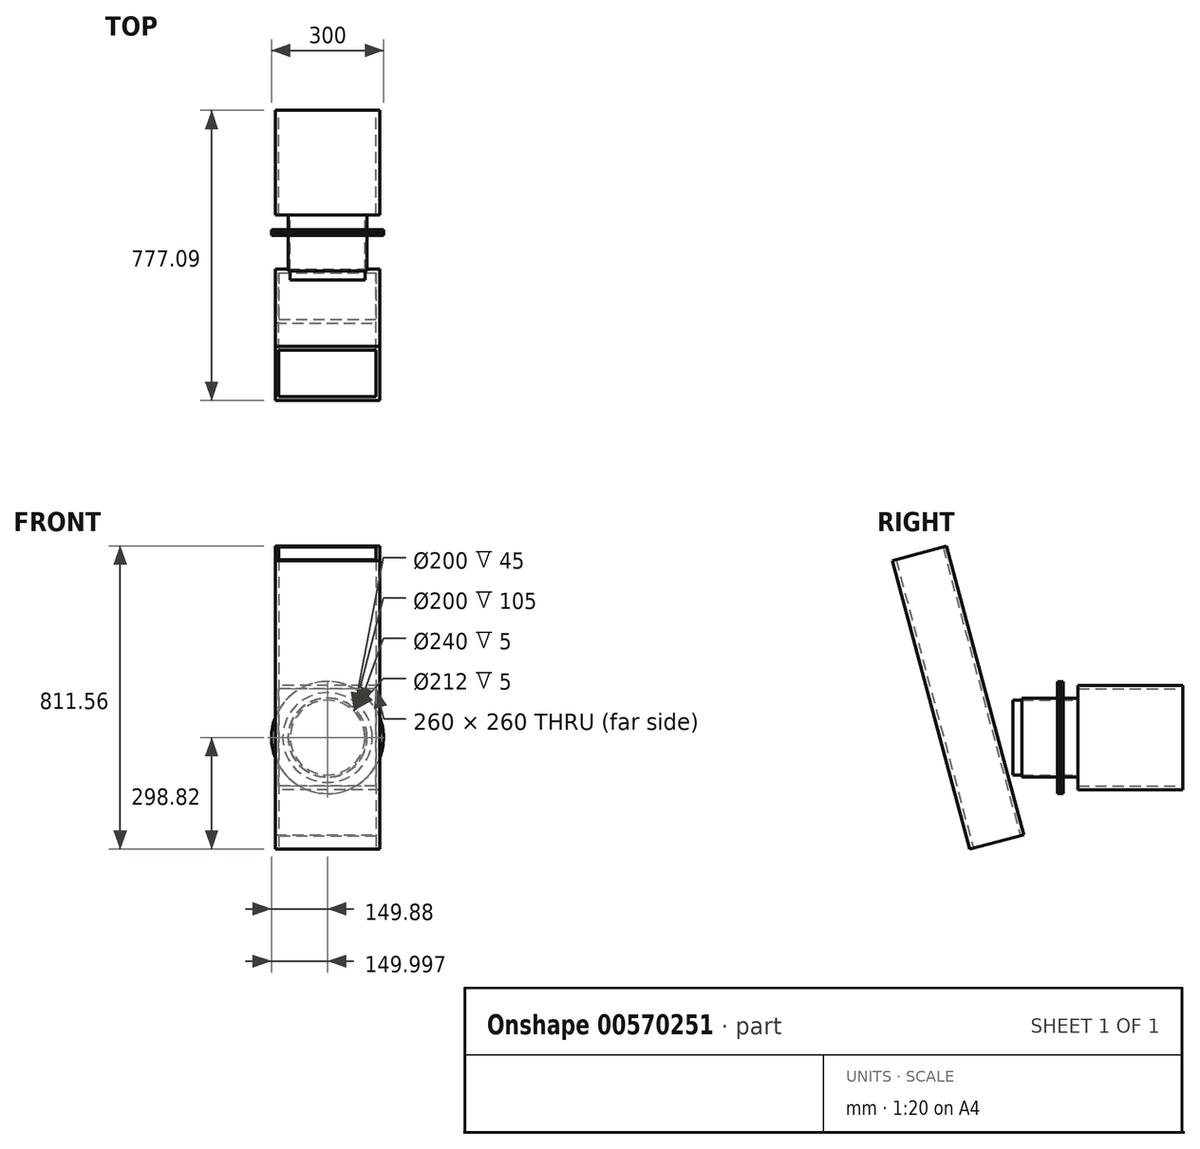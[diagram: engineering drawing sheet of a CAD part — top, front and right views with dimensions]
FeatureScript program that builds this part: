
annotation { "Feature Type Name" : "Feature", "Feature Type Description" : "" }
export const myFeature = defineFeature(function(context is Context, id is Id, definition is map)
    precondition{}
    {
        {
            var Q0;
            Q0=qCreatedBy(makeId("Front.planeOp"),FACE);
            var sketch = newSketch(context, id + "F0", { "sketchPlane" : qUnion([Q0])});
            skLineSegment(sketch, "E0.bottom", {"start": v(0, 0) * mm, "end": v(-280, 0) * mm});
            skLineSegment(sketch, "E0.top", {"start": v(0, 280) * mm, "end": v(-280, 280) * mm});
            skLineSegment(sketch, "E0.left", {"start": v(0, 0) * mm, "end": v(0, 280) * mm});
            skLineSegment(sketch, "E0.right", {"start": v(-280, 0) * mm, "end": v(-280, 280) * mm});
            skLineSegment(sketch, "E1.0", {"start": v(-10, 270) * mm, "end": v(-270, 270) * mm});
            skLineSegment(sketch, "E1.1", {"start": v(-10, 10) * mm, "end": v(-10, 270) * mm});
            skLineSegment(sketch, "E1.2", {"start": v(-10, 10) * mm, "end": v(-270, 10) * mm});
            skLineSegment(sketch, "E1.3", {"start": v(-270, 10) * mm, "end": v(-270, 270) * mm});
            skSolve(sketch);
        }
        {
            var Q0;
            Q0 = qSketchRegion(id + "F0", true);
            extrude(context, id + "F1", {"entities" : qUnion([Q0]), "depth" : 280 * mm, "offsetDistance" : 25 * mm});
        }
        {
            var Q0;
            Q0=makeQuery(id+"F1.opExtrude","CAP_FACE",FACE,{"disambiguationData":[OSD([sQuery(id+"F0.wireOp",EDGE,"E0.bottom"),sQuery(id+"F0.wireOp",EDGE,"E0.top"),sQuery(id+"F0.wireOp",EDGE,"E0.left"),sQuery(id+"F0.wireOp",EDGE,"E0.right"),sQuery(id+"F0.wireOp",EDGE,"E1.0"),sQuery(id+"F0.wireOp",EDGE,"E1.1"),sQuery(id+"F0.wireOp",EDGE,"E1.2"),sQuery(id+"F0.wireOp",EDGE,"E1.3")])],"isStart":false});
            var sketch = newSketch(context, id + "F2", { "sketchPlane" : qUnion([Q0])});
            skPoint(sketch, "E2.endSnap0", {"position": v(0, 140) * mm});
            skCircle(sketch, "E3", {"center": v(-139.88, 140) * mm, "radius": 100 * mm});
            skCircle(sketch, "E4.0", {"center": v(-139.88, 140) * mm, "radius": 105 * mm});
            skSolve(sketch);
        }
        {
            var Q0;
            Q0 = qSketchRegion(id + "F2", true);
            extrude(context, id + "F3", {"entities" : qUnion([Q0]), "depth" : 40 * mm, "offsetDistance" : 25 * mm});
        }
        {
            var Q0;
            Q0=makeQuery(id+"F3.opExtrude","CAP_FACE",FACE,{"disambiguationData":[OSD([sQuery(id+"F2.wireOp",EDGE,"E3"),sQuery(id+"F2.wireOp",EDGE,"E4.0")])],"isStart":false});
            var sketch = newSketch(context, id + "F4", { "sketchPlane" : qUnion([Q0])});
            skCircle(sketch, "E5", {"center": v(-139.88, 140) * mm, "radius": 150 * mm});
            skCircle(sketch, "E6.0", {"center": v(-139.88, 140) * mm, "radius": 100 * mm});
            skSolve(sketch);
        }
        {
            var Q0;
            Q0 = qSketchRegion(id + "F4", true);
            extrude(context, id + "F5", {"entities" : qUnion([Q0]), "operationType" : NewBodyOperationType.ADD, "depth" : 5 * mm, "offsetDistance" : 25 * mm});
        }
        {
            var Q0;
            Q0=makeQuery(id+"F5.opExtrude","CAP_FACE",FACE,{"disambiguationData":[OSD([sQuery(id+"F4.wireOp",EDGE,"E5"),sQuery(id+"F4.wireOp",EDGE,"E6.0")])],"isStart":false});
            var sketch = newSketch(context, id + "F6", { "sketchPlane" : qUnion([Q0])});
            skCircle(sketch, "E7", {"center": v(-139.88, 140) * mm, "radius": 150 * mm});
            skCircle(sketch, "E8", {"center": v(-139.88, 140) * mm, "radius": 120 * mm});
            skSolve(sketch);
        }
        {
            var Q0;
            Q0 = qSketchRegion(id + "F6", true);
            extrude(context, id + "F7", {"entities" : qUnion([Q0]), "depth" : 5 * mm, "offsetDistance" : 25 * mm});
        }
        {
            var Q0;
            Q0=makeQuery(id+"F5.opExtrude","CAP_FACE",FACE,{"disambiguationData":[OSD([sQuery(id+"F4.wireOp",EDGE,"E5"),sQuery(id+"F4.wireOp",EDGE,"E6.0")])],"isStart":false});
            var sketch = newSketch(context, id + "F8", { "sketchPlane" : qUnion([Q0])});
            skCircle(sketch, "E9", {"center": v(-139.88, 140) * mm, "radius": 100 * mm});
            skCircle(sketch, "E10", {"center": v(-139.88, 140) * mm, "radius": 120 * mm});
            skSolve(sketch);
        }
        {
            var Q0;
            Q0 = qSketchRegion(id + "F8", true);
            extrude(context, id + "F9", {"entities" : qUnion([Q0]), "depth" : 5 * mm, "offsetDistance" : 25 * mm});
        }
        {
            var Q0;
            Q0=makeQuery(id+"F9.opExtrude","CAP_FACE",FACE,{"disambiguationData":[OSD([sQuery(id+"F8.wireOp",EDGE,"E9"),sQuery(id+"F8.wireOp",EDGE,"E10")])],"isStart":false});
            var sketch = newSketch(context, id + "F10", { "sketchPlane" : qUnion([Q0])});
            skCircle(sketch, "E11", {"center": v(-139.88, 140) * mm, "radius": 100 * mm});
            skCircle(sketch, "E12.0", {"center": v(-139.88, 140) * mm, "radius": 105 * mm});
            skSolve(sketch);
        }
        {
            var Q0;
            Q0 = qSketchRegion(id + "F10", true);
            extrude(context, id + "F11", {"entities" : qUnion([Q0]), "operationType" : NewBodyOperationType.ADD, "depth" : 100 * mm, "offsetDistance" : 25 * mm});
        }
        {
            var Q0;
            Q0=makeQuery(id+"F7.opExtrude","CAP_FACE",FACE,{"disambiguationData":[OSD([sQuery(id+"F6.wireOp",EDGE,"E7"),sQuery(id+"F6.wireOp",EDGE,"E8")])],"isStart":false});
            var sketch = newSketch(context, id + "F12", { "sketchPlane" : qUnion([Q0])});
            skCircle(sketch, "E13", {"center": v(-139.88, 140) * mm, "radius": 150 * mm});
            skCircle(sketch, "E14.0", {"center": v(-139.88, 140) * mm, "radius": 106 * mm});
            skSolve(sketch);
        }
        {
            var Q0;
            Q0 = qSketchRegion(id + "F12", true);
            extrude(context, id + "F13", {"entities" : qUnion([Q0]), "depth" : 5 * mm, "offsetDistance" : 25 * mm});
        }
        {
            var Q0;
            Q0=makeQuery(id+"F1.opExtrude","SWEPT_FACE",FACE,{"disambiguationData":[OSD([sQuery(id+"F0.wireOp",EDGE,"E0.top")])]});
            var sketch = newSketch(context, id + "F14", { "sketchPlane" : qUnion([Q0])});
            skLineSegment(sketch, "E15.bottom", {"start": v(-280, -425.14) * mm, "end": v(0, -425.14) * mm});
            skLineSegment(sketch, "E15.top", {"start": v(-280, -575.14) * mm, "end": v(0, -575.14) * mm});
            skLineSegment(sketch, "E15.left", {"start": v(-280, -425.14) * mm, "end": v(-280, -575.14) * mm});
            skLineSegment(sketch, "E15.right", {"start": v(0, -425.14) * mm, "end": v(0, -575.14) * mm});
            skLineSegment(sketch, "E16.0", {"start": v(-270, -435.14) * mm, "end": v(-270, -565.14) * mm});
            skLineSegment(sketch, "E16.1", {"start": v(-270, -435.14) * mm, "end": v(-10, -435.14) * mm});
            skLineSegment(sketch, "E16.2", {"start": v(-10, -435.14) * mm, "end": v(-10, -565.14) * mm});
            skLineSegment(sketch, "E16.3", {"start": v(-270, -565.14) * mm, "end": v(-10, -565.14) * mm});
            skSolve(sketch);
        }
        {
            var Q0;
            Q0 = qSketchRegion(id + "F14", true);
            extrude(context, id + "F15", {"entities" : qUnion([Q0]), "endBound" : BoundingType.SYMMETRIC, "depth" : 800 * mm, "offsetDistance" : 25 * mm});
        }
        {
            var Q0;
            Q0=makeQuery(id+"F15.opExtrude","SWEPT_BODY",BODY,{"disambiguationData":[OSD([sQuery(id+"F14.wireOp",EDGE,"E15.bottom"),sQuery(id+"F14.wireOp",EDGE,"E15.top"),sQuery(id+"F14.wireOp",EDGE,"E15.left"),sQuery(id+"F14.wireOp",EDGE,"E15.right"),sQuery(id+"F14.wireOp",EDGE,"E16.0"),sQuery(id+"F14.wireOp",EDGE,"E16.1"),sQuery(id+"F14.wireOp",EDGE,"E16.2"),sQuery(id+"F14.wireOp",EDGE,"E16.3")])]});
            var Q1;
            Q1=makeQuery(id+"F15.opExtrude","CAP_EDGE",EDGE,{"disambiguationData":[OSD([sQuery(id+"F14.wireOp",EDGE,"E15.bottom")])],"isStart":true});
            transform(context, id + "F16", {"entities" : qUnion([Q0]), "transformType" : TransformType.ROTATION, "transformAxis" : qUnion([Q1]), "angle" : 15 * degree, "makeCopy" : false});
        }
        {
            var Q0;
            Q0=makeQuery(id+"F11.opExtrude","CAP_FACE",FACE,{"disambiguationData":[OSD([sQuery(id+"F10.wireOp",EDGE,"E11"),sQuery(id+"F10.wireOp",EDGE,"E12.0")])],"isStart":false});
            var sketch = newSketch(context, id + "F17", { "sketchPlane" : qUnion([Q0])});
            skCircle(sketch, "E17", {"center": v(-139.88, 140) * mm, "radius": 100 * mm});
            skSolve(sketch);
        }
        {
            var Q0;
            Q0 = qSketchRegion(id + "F17", true);
            extrude(context, id + "F18", {"entities" : qUnion([Q0]), "depth" : 25 * mm, "offsetDistance" : 25 * mm});
        }
    });
